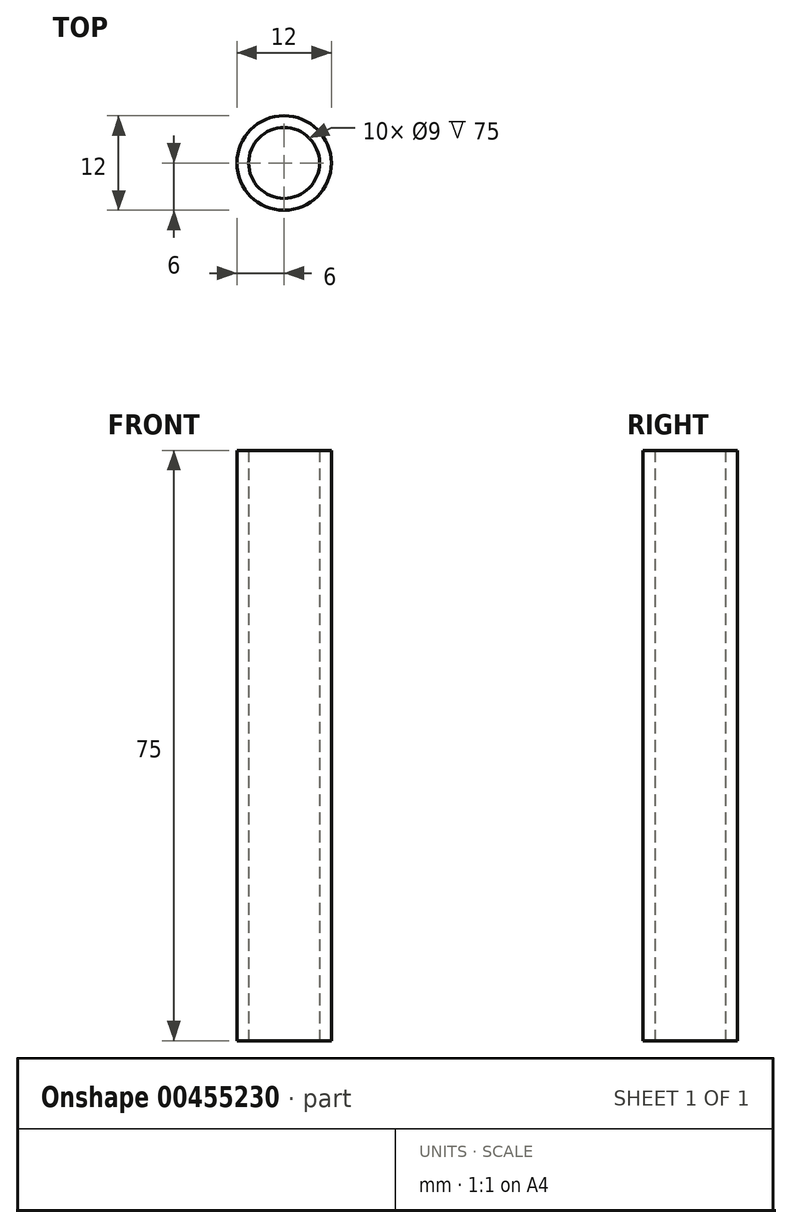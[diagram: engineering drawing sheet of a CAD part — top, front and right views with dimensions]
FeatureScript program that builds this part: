
annotation { "Feature Type Name" : "Feature", "Feature Type Description" : "" }
export const myFeature = defineFeature(function(context is Context, id is Id, definition is map)
    precondition{}
    {
        {
            var Q0;
            Q0=qCreatedBy(makeId("Top.planeOp"),FACE);
            var sketch = newSketch(context, id + "F0", { "sketchPlane" : qUnion([Q0])});
            skCircle(sketch, "E0", {"center": v(0, 0) * mm, "radius": 6 * mm});
            skCircle(sketch, "E1", {"center": v(0, 0) * mm, "radius": 4.5 * mm});
            skSolve(sketch);
        }
        {
            var Q0;
            Q0=makeQuery(id+"F0.imprint","IMPRINT",FACE,{"disambiguationData":[TD([[makeQuery(id+"F0.imprint","IMPRINT",EDGE,{"derivedFrom":sQuery(id+"F0.wireOp",EDGE,"E0")}),1.0]])]});
            extrude(context, id + "F1", {"entities" : qUnion([Q0]), "depth" : 75 * mm});
        }
    });
